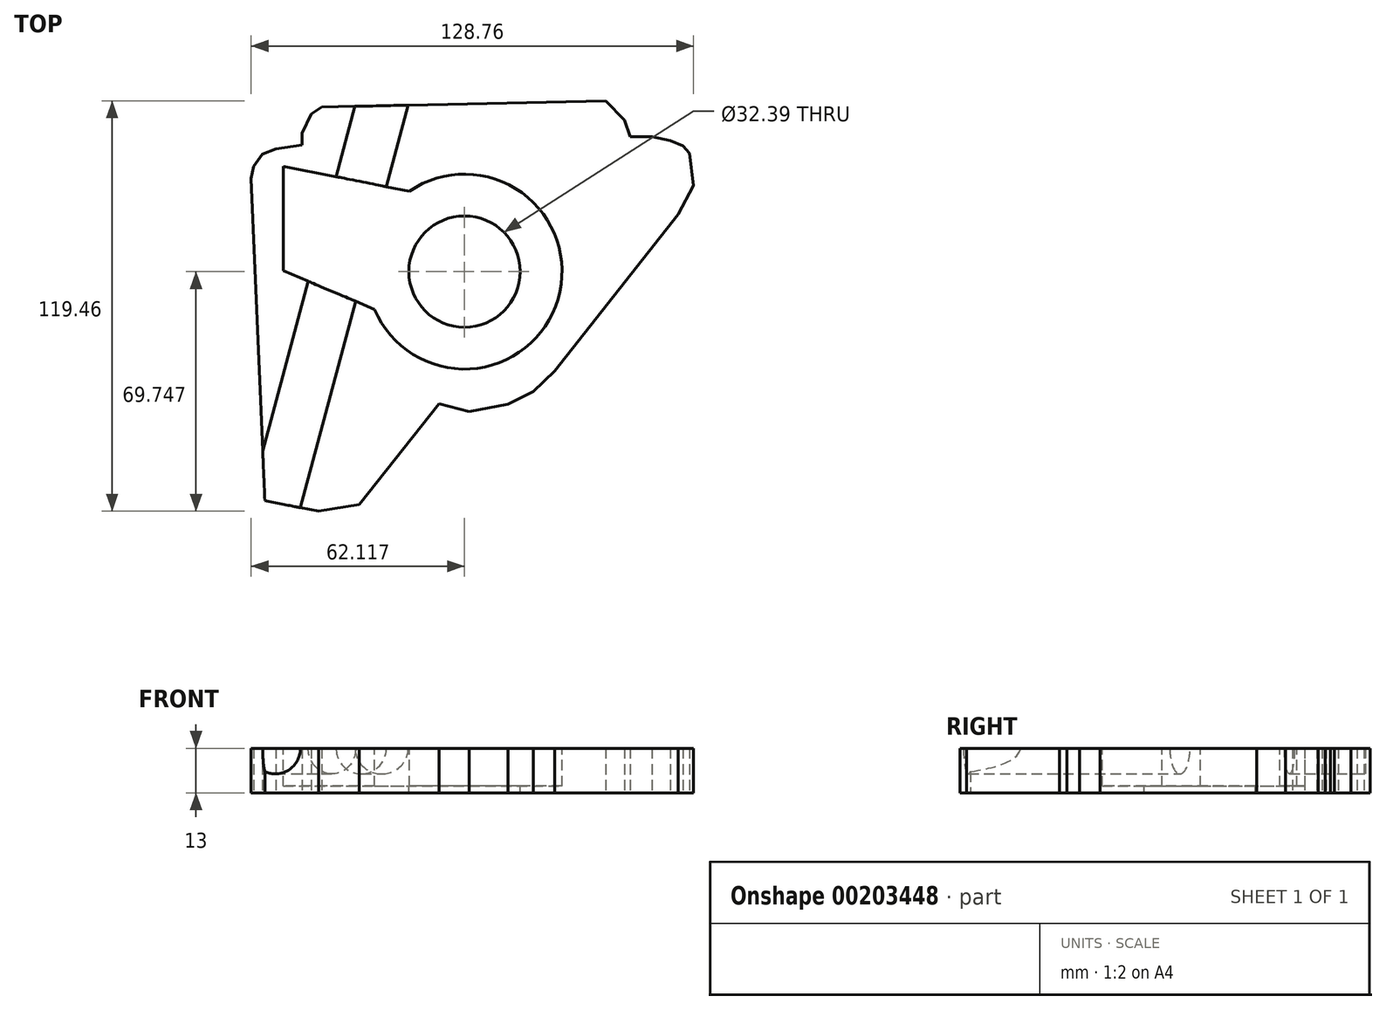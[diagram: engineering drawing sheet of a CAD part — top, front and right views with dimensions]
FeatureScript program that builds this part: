
annotation { "Feature Type Name" : "Feature", "Feature Type Description" : "" }
export const myFeature = defineFeature(function(context is Context, id is Id, definition is map)
    precondition{}
    {
        {
            var Q0;
            Q0=qCreatedBy(makeId("Top.planeOp"),FACE);
            var sketch = newSketch(context, id + "F0", { "sketchPlane" : qUnion([Q0])});
            skLineSegment(sketch, "E0", {"start": v(-8.8, -31.39) * mm, "end": v(0, -33.7) * mm});
            skLineSegment(sketch, "E1", {"start": v(0, -33.7) * mm, "end": v(11.3, -31.58) * mm});
            skLineSegment(sketch, "E2", {"start": v(11.3, -31.58) * mm, "end": v(18.65, -27.9) * mm});
            skLineSegment(sketch, "E3", {"start": v(18.65, -27.9) * mm, "end": v(24.83, -21.92) * mm});
            skLineSegment(sketch, "E4", {"start": v(24.83, -21.92) * mm, "end": v(60.8, 23.7) * mm});
            skLineSegment(sketch, "E5", {"start": v(60.8, 23.7) * mm, "end": v(65.24, 32.02) * mm});
            skLineSegment(sketch, "E6", {"start": v(65.24, 32.02) * mm, "end": v(64.06, 41.53) * mm});
            skLineSegment(sketch, "E7", {"start": v(64.06, 41.53) * mm, "end": v(62.24, 43.6) * mm});
            skLineSegment(sketch, "E8", {"start": v(62.24, 43.6) * mm, "end": v(58.46, 45.18) * mm});
            skLineSegment(sketch, "E9", {"start": v(58.46, 45.18) * mm, "end": v(53.1, 46.28) * mm});
            skLineSegment(sketch, "E10", {"start": v(53.1, 46.28) * mm, "end": v(46.77, 46.28) * mm});
            skLineSegment(sketch, "E11", {"start": v(46.77, 46.28) * mm, "end": v(45.19, 51.15) * mm});
            skLineSegment(sketch, "E12", {"start": v(45.19, 51.15) * mm, "end": v(39.7, 56.75) * mm});
            skLineSegment(sketch, "E13", {"start": v(39.7, 56.75) * mm, "end": v(-42.98, 54.93) * mm});
            skLineSegment(sketch, "E14", {"start": v(-42.98, 54.93) * mm, "end": v(-46.03, 52.86) * mm});
            skLineSegment(sketch, "E15", {"start": v(-46.03, 52.86) * mm, "end": v(-48.7, 47.38) * mm});
            skLineSegment(sketch, "E16", {"start": v(-48.7, 47.38) * mm, "end": v(-48.7, 43.84) * mm});
            skLineSegment(sketch, "E17", {"start": v(-48.7, 43.84) * mm, "end": v(-56.26, 42.75) * mm});
            skLineSegment(sketch, "E18", {"start": v(-56.26, 42.75) * mm, "end": v(-60.28, 41.17) * mm});
            skLineSegment(sketch, "E19", {"start": v(-60.28, 41.17) * mm, "end": v(-62.84, 37.63) * mm});
            skLineSegment(sketch, "E20", {"start": v(-62.84, 37.63) * mm, "end": v(-63.52, 34.1) * mm});
            skLineSegment(sketch, "E21", {"start": v(-63.52, 34.1) * mm, "end": v(-59.53, -59.65) * mm});
            skLineSegment(sketch, "E22", {"start": v(-59.53, -59.65) * mm, "end": v(-57.75, -60) * mm});
            skLineSegment(sketch, "E23", {"start": v(-57.75, -60) * mm, "end": v(-43.86, -62.7) * mm});
            skLineSegment(sketch, "E24", {"start": v(-43.86, -62.7) * mm, "end": v(-32.08, -60.81) * mm});
            skLineSegment(sketch, "E25", {"start": v(-32.08, -60.81) * mm, "end": v(-8.8, -31.39) * mm});
            skSolve(sketch);
        }
        {
            var Q0;
            Q0 = qSketchRegion(id + "F0", true);
            extrude(context, id + "F1", {"entities" : qUnion([Q0]), "depth" : 13 * mm});
        }
        {
            var Q0;
            Q0=makeQuery(id+"F1.opExtrude","CAP_FACE",FACE,{"disambiguationData":[OSD([sQuery(id+"F0.wireOp",EDGE,"E0"),sQuery(id+"F0.wireOp",EDGE,"E1"),sQuery(id+"F0.wireOp",EDGE,"E2"),sQuery(id+"F0.wireOp",EDGE,"E3"),sQuery(id+"F0.wireOp",EDGE,"E4"),sQuery(id+"F0.wireOp",EDGE,"E5"),sQuery(id+"F0.wireOp",EDGE,"E6"),sQuery(id+"F0.wireOp",EDGE,"E7"),sQuery(id+"F0.wireOp",EDGE,"E8"),sQuery(id+"F0.wireOp",EDGE,"E9"),sQuery(id+"F0.wireOp",EDGE,"E10"),sQuery(id+"F0.wireOp",EDGE,"E11"),sQuery(id+"F0.wireOp",EDGE,"E12"),sQuery(id+"F0.wireOp",EDGE,"E13"),sQuery(id+"F0.wireOp",EDGE,"E14"),sQuery(id+"F0.wireOp",EDGE,"E15"),sQuery(id+"F0.wireOp",EDGE,"E16"),sQuery(id+"F0.wireOp",EDGE,"E17"),sQuery(id+"F0.wireOp",EDGE,"E18"),sQuery(id+"F0.wireOp",EDGE,"E19"),sQuery(id+"F0.wireOp",EDGE,"E20"),sQuery(id+"F0.wireOp",EDGE,"E21"),sQuery(id+"F0.wireOp",EDGE,"E22"),sQuery(id+"F0.wireOp",EDGE,"E23"),sQuery(id+"F0.wireOp",EDGE,"E24"),sQuery(id+"F0.wireOp",EDGE,"E25")])],"isStart":false});
            var sketch = newSketch(context, id + "F2", { "sketchPlane" : qUnion([Q0])});
            skCircle(sketch, "E26", {"center": v(-1.4, 7.04) * mm, "radius": 16.2 * mm});
            skCircle(sketch, "E27", {"center": v(-1.4, 7.04) * mm, "radius": 28.37 * mm});
            skLineSegment(sketch, "E28", {"start": v(-27.56, -3.95) * mm, "end": v(-54.2, 7.34) * mm});
            skLineSegment(sketch, "E29", {"start": v(-54.2, 7.34) * mm, "end": v(-54.2, 37.72) * mm});
            skLineSegment(sketch, "E30", {"start": v(-54.2, 37.72) * mm, "end": v(-17.45, 30.43) * mm});
            skPoint(sketch, "E31", {"position": v(-7.5, 43.2) * mm});
            skPoint(sketch, "E32", {"position": v(-22.5, -23.2) * mm});
            skSolve(sketch);
        }
        {
            var Q0;
            Q0=makeQuery(id+"F2.imprint","IMPRINT",FACE,{"disambiguationData":[TD([[makeQuery(id+"F2.imprint","IMPRINT",EDGE,{"derivedFrom":sQuery(id+"F2.wireOp",EDGE,"E26")}),1.0]])]});
            extrude(context, id + "F3", {"entities" : qUnion([Q0]), "operationType" : NewBodyOperationType.REMOVE, "endBound" : BoundingType.UP_TO_NEXT, "oppositeDirection" : true, "depth" : 25 * mm});
        }
        {
            var Q0;
            Q0=makeQuery(id+"F2.imprint","IMPRINT",FACE,{"disambiguationData":[TD([[makeQuery(id+"F2.imprint","IMPRINT",EDGE,{"derivedFrom":sQuery(id+"F2.wireOp",EDGE,"E26")}),-1.0]])]});
            var Q1;
            {var subQ0=sQuery(id+"F2.wireOp",EDGE,"E28");Q1=makeQuery(id+"F2.imprint","IMPRINT",FACE,{"disambiguationData":[TD([[makeQuery(id+"F2.imprint","IMPRINT",EDGE,{"derivedFrom":subQ0}),-1.0]])]});}
            extrude(context, id + "F4", {"entities" : qUnion([Q0, Q1]), "operationType" : NewBodyOperationType.REMOVE, "oppositeDirection" : true, "depth" : 11 * mm});
        }
        {
            var Q0;
            {var subQ1=sQuery(id+"F2.wireOp",EDGE,"E28");Q0=makeQuery(id+"F2.imprint","IMPRINT",FACE,{"disambiguationData":[TD([[makeQuery(id+"F2.imprint","IMPRINT",EDGE,{"derivedFrom":subQ1}),1.0]])]});}
            var sketch = newSketch(context, id + "F5", { "sketchPlane" : qUnion([Q0])});
            skPoint(sketch, "E33", {"position": v(-33.29, 55.42) * mm});
            skPoint(sketch, "E34", {"position": v(-17.78, 55.42) * mm});
            skPoint(sketch, "E35", {"position": v(-23.08, 34.27) * mm});
            skLineSegment(sketch, "E36", {"start": v(-23.08, 34.27) * mm, "end": v(-17.78, 55.42) * mm, "construction": true});
            skLineSegment(sketch, "E37", {"start": v(-17.78, 55.42) * mm, "end": v(3.44, 50.1) * mm, "construction": true});
            skSolve(sketch);
        }
        {
            var Q0;
            Q0=makeQuery(id+"F1.opExtrude","SWEPT_FACE",FACE,{"disambiguationData":[OSD([sQuery(id+"F0.wireOp",EDGE,"E13")])]});
            var sketch = newSketch(context, id + "F6", { "sketchPlane" : qUnion([Q0])});
            skPoint(sketch, "E38.0", {"position": v(32.06, 13) * mm});
            skPoint(sketch, "E39.0", {"position": v(16.55, 13) * mm});
            skLineSegment(sketch, "E40", {"start": v(32.06, 13) * mm, "end": v(16.55, 13) * mm, "construction": true});
            skPoint(sketch, "E41", {"position": v(24.3, 13) * mm});
            skSolve(sketch);
        }
        {
            var Q0;
            {var subQ0=sQuery(id+"F0.wireOp",EDGE,"E13");Q0=makeQuery(id+"F6.imprint","IMPRINT",FACE,{"disambiguationData":[TD([[makeQuery(id+"F6.imprint","IMPRINT",EDGE,{"derivedFrom":makeQuery(id+"F1.opExtrude","CAP_EDGE",EDGE,{"disambiguationData":[OSD([subQ0])],"isStart":true})}),1.0]])]});}
            var sketch = newSketch(context, id + "F7", { "sketchPlane" : qUnion([Q0])});
            skPoint(sketch, "E42.0", {"position": v(16.55, 13) * mm});
            skLineSegment(sketch, "E43", {"start": v(16.55, 13) * mm, "end": v(16.55, 0) * mm});
            skSolve(sketch);
        }
        {
            var Q0;
            Q0=sQuery(id+"F7.wireOp",EDGE,"E43");
            cPlane(context, id + "F8", {"entities" : qUnion([Q0]), "cplaneType" : CPlaneType.LINE_ANGLE, "offset" : 25 * mm, "angle" : 75 * degree, "oppositeDirection" : true, "width" : 150 * mm, "height" : 150 * mm});
        }
        {
            var Q0;
            Q0=qCreatedBy(id+"F8.planeOp",FACE);
            var sketch = newSketch(context, id + "F9", { "sketchPlane" : qUnion([Q0])});
            skPoint(sketch, "E44.0", {"position": v(-31.54, 13) * mm});
            skPoint(sketch, "E45.0", {"position": v(-38.98, 13) * mm});
            skCircle(sketch, "E46", {"center": v(-38.98, 13) * mm, "radius": 7.44 * mm});
            skSolve(sketch);
        }
        {
            var Q0;
            Q0 = qSketchRegion(id + "F9", true);
            extrude(context, id + "F10", {"entities" : qUnion([Q0]), "operationType" : NewBodyOperationType.REMOVE, "endBound" : BoundingType.THROUGH_ALL, "depth" : 25 * mm});
        }
    });
